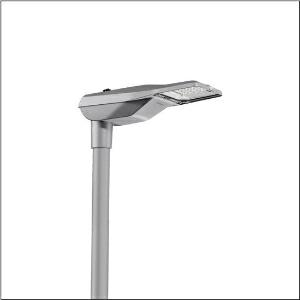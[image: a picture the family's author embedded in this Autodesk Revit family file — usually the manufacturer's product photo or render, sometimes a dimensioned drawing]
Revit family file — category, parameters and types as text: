
# Revit family: streetlight_sl_21_micro___st0_8a_5xe1c33s08db_f35f
name_source: partatom
category: Lighting Fixtures
units: mm (PartAtom-declared; Revit-internal decimal feet)

## family parameters
Cut with Voids When Loaded = No
Host = Face
Light Source = No
Part Type = Normal
Room Calculation Point = No
Round Connector Dimension = Use Diameter
Shared = No

## types (1)
- --- (1 x LED, 5110 lm, 39.1 W, 3000K)
    Apparent Load = 39 VA
    CIE Flux Codes = 38 75 97 100 100
    Color Rendering = 70
    Color Temperature = 3000K
    Default Elevation = 1800 mm
    Description = Streetlight SL 21 micro, mast luminaire, primary light control with lens, of PMMA, primary optical cover: cover, of toughened safety glass, transparent, light distribution: ST0.8a, light emission: direct distribution, primary light characteristic: asymmetric, installation type: side-entry, post-top, LED, High Power LED, rated luminous flux: 5.110lm, luminous efficacy: 131lm/W, light colour: 730, colour temperature: 3000K, control gear: D4i, control: flexible luminous flux parameterisation, time-dependent luminous flux control, constant luminous flux control, overheat protection, pre-setting: logarithmic dimming characteristic, mains connection: 220..240V, AC, 50/60Hz, start of lifetime: 39W, end of service life: 41W, reduction: 18W, luminaire housing, of diecast aluminium, powder-coated, Siteco® metallic grey (DB 702S), corrosivity category C5 mid according to DIN EN ISO 12944, please order mast flange separately, inclination adjustable: 0°, 5°, 10°, 15°, sealing non-destructively replaceable, multi-level sealing system, length: 528mm, width: 235mm, height: 110mm, mast flange for spigot size: 42mm (side-entry): 5XC10008XM4, 60/48mm (side-entry/post-top): 5XC10108XM2, 76/60mm (side-entry/post-top): 5XC10108XM1, Smart Interface above, protection rating (complete): IP66, insulation class (complete): insulation class II (safety insulation), certification: CE, ENEC, ENEC+, VDE, impact resistance: IK09, permissible operating ambient temperature for outdoor applications: -40..+50°C, standard-compliant lighting for roads and squares, packaging unit: 1 piece

Light Distribution: ST0.8a
    Height = 110 mm
    Lamp = 1 x LED
    Lamp Light Flux = 5110 lm
    Lamp Power = 39.1 W
    Lamp count = 1
    Length = 528 mm
    Luminous efficacy = 131 lm/W
    Manufacturer = Siteco
    ModVariant = No
    Model = 5XE1C33S08DB
    Number of Poles = 1
    OnlyDefault = Yes
    Power Factor = 1
    Product Name = Streetlight SL 21 micro | ST0.8a
    Product group = mast luminaire | pylon top
    ProductGroupID = 6100
    Protection Class = Protection class II
    Protection Degree = IP 66
    RLX_Detail_Level = 1
    RLX_Emergency_Light_Flux = 0 lm
    RLX_Emergency_Type = 0
    RLX_Emergency_Type_DB = No
    RlxData = <blob elided: 98317 chars, md5=b2dc0cc0>
    Socket = socket
    Standby Power = 0 W
    System Light Flux = 5110 lm
    System Power = 39 W
    Type Comments = factory setting: luminous flux: 100 % | dim-lin: 254 | 765 mA
    Type Image = l_1277292.jpg
    URL = http://relux.com
    VarID = @adj_150096
    Voltage = 0 V
    Weight = 0.00 kg
    Width = 235 mm

## geometry (parser evidence)
native form markers: Blend x4, Sweep x12
no freeform markers — native parametric forms only
